# Revit family: DeckAnchor No-Hub connection - ductile iron
name_source: partatom
category: Pipe Fittings
units: mm (PartAtom-declared; Revit-internal decimal feet)

## family parameters
Always vertical = Yes
Cut with Voids When Loaded = No
Part Type = Elbow
Round Connector Dimension = Use Diameter
Shared = No
Work Plane-Based = No

## types (4) — shared parameters
Default Elevation = 0' - 0"
Manufacturer = Sioux Chief
URL = www.siouxchief.com

## per-type parameters (varying)
| type | Bottom Radius | Connector Diameter | Description | Inlet Length | Model | Tab Radius | Top Radius |
| 836-2 DeckAnchor - 2" No-Hub | 0' - 5 1/4" | 0' - 2" | DeckAnchor 2" No-Hub connection - ductile iron | 0' - 5 5/8" | 836-2 | 0' - 4 7/32" | 0' - 1 3/16" |
| 836-3 DeckAnchor - 3" No-Hub | 0' - 5 1/4" | 0' - 3" | DeckAnchor 3" No-Hub connection - ductile iron | 0' - 5 5/8" | 836-3 | 0' - 4 7/32" | 0' - 1 11/16" |
| 836-4 DeckAnchor - 4" No-Hub | 0' - 5 1/4" | 0' - 4" | DeckAnchor 4" No-Hub connection - ductile iron | 0' - 5 5/8" | 836-4 | 0' - 4 7/32" | 0' - 2 3/16" |
| 836-6 DeckAnchor - 6" No-Hub | 0' - 6 1/4" | 0' - 6" | DeckAnchor 6" No-Hub connection - ductile iron | 0' - 5 1/4" | 836-6 | 0' - 5 7/32" | 0' - 3 5/32" |

## geometry (parser evidence)
native form markers: Sweep x2
no freeform markers — native parametric forms only
